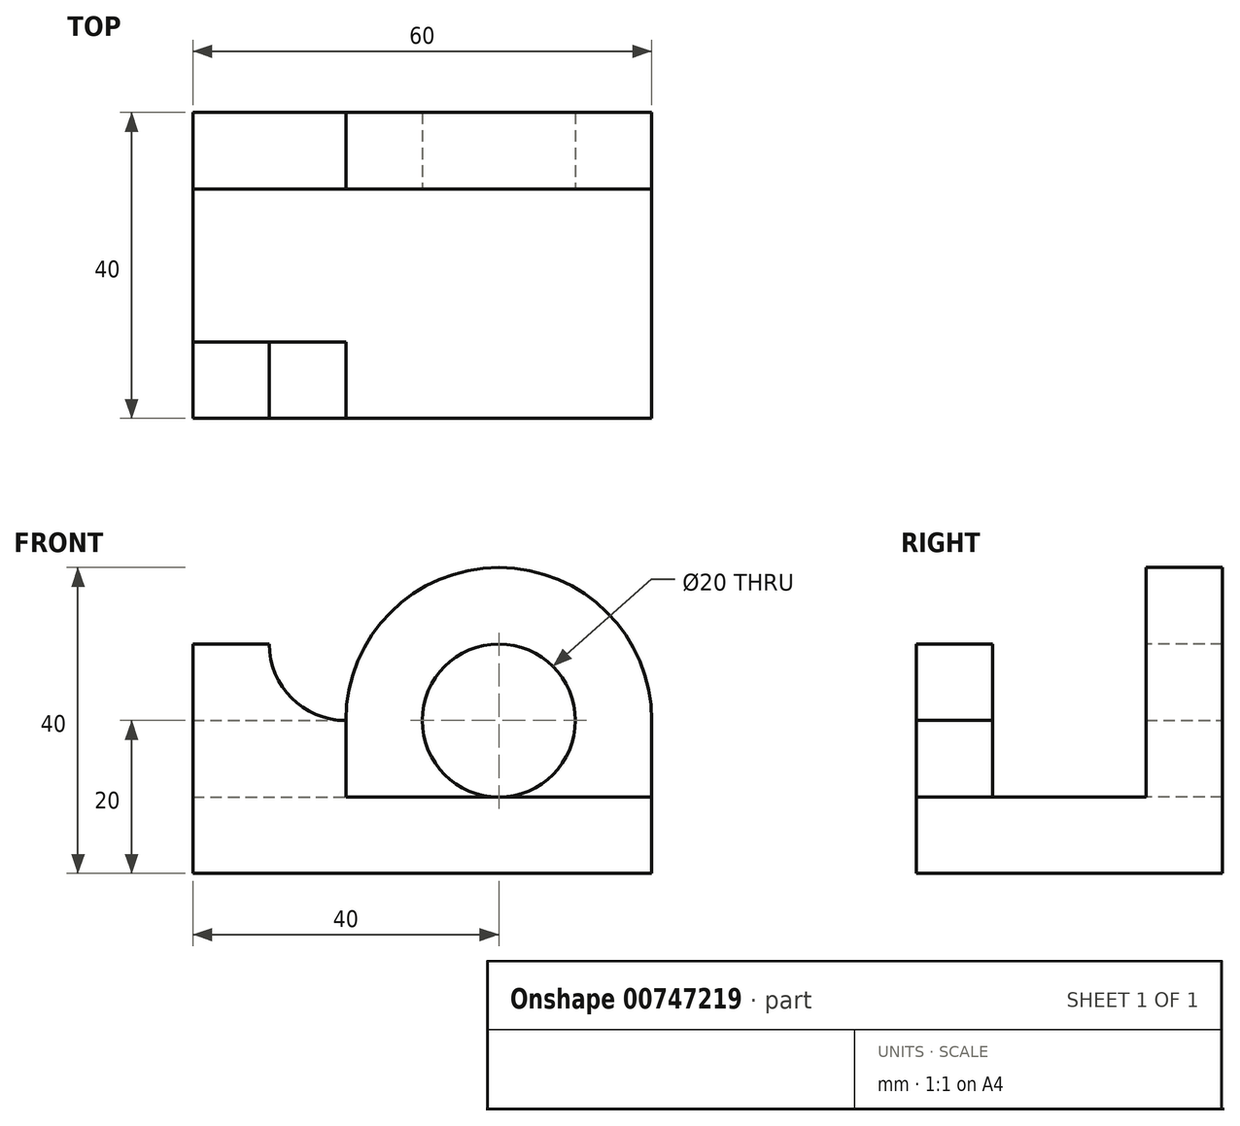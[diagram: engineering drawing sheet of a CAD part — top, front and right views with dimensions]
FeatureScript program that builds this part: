
annotation { "Feature Type Name" : "Feature", "Feature Type Description" : "" }
export const myFeature = defineFeature(function(context is Context, id is Id, definition is map)
    precondition{}
    {
        {
            var Q0;
            Q0=qCreatedBy(makeId("Front.planeOp"),FACE);
            var sketch = newSketch(context, id + "F0", { "sketchPlane" : qUnion([Q0])});
            skLineSegment(sketch, "E0", {"start": v(0, 0) * mm, "end": v(60, 0) * mm});
            skLineSegment(sketch, "E1", {"start": v(60, 0) * mm, "end": v(60, 40) * mm});
            skLineSegment(sketch, "E2", {"start": v(60, 40) * mm, "end": v(0, 40) * mm});
            skLineSegment(sketch, "E3", {"start": v(0, 40) * mm, "end": v(0, 0) * mm});
            skSolve(sketch);
        }
        {
            var Q0;
            Q0=makeQuery(id+"F0.imprint","IMPRINT",FACE,{"disambiguationData":[TD([[makeQuery(id+"F0.imprint","IMPRINT",EDGE,{"derivedFrom":sQuery(id+"F0.wireOp",EDGE,"E0")}),1.0]])]});
            extrude(context, id + "F1", {"entities" : qUnion([Q0]), "depth" : 40 * mm, "offsetDistance" : 25 * mm});
        }
        {
            var Q0;
            Q0=makeQuery(id+"F1.opExtrude","SWEPT_FACE",FACE,{"disambiguationData":[OSD([sQuery(id+"F0.wireOp",EDGE,"E1")])]});
            var sketch = newSketch(context, id + "F2", { "sketchPlane" : qUnion([Q0])});
            skLineSegment(sketch, "E4", {"start": v(-40, 40) * mm, "end": v(-40, 30) * mm});
            skLineSegment(sketch, "E5", {"start": v(-40, 30) * mm, "end": v(-30, 30) * mm});
            skLineSegment(sketch, "E6", {"start": v(-30, 30) * mm, "end": v(-30, 10) * mm});
            skLineSegment(sketch, "E7", {"start": v(-30, 10) * mm, "end": v(-10, 10) * mm});
            skLineSegment(sketch, "E8", {"start": v(-10, 10) * mm, "end": v(-10, 40) * mm});
            skLineSegment(sketch, "E9", {"start": v(-10, 40) * mm, "end": v(-40, 40) * mm});
            skSolve(sketch);
        }
        {
            var Q0;
            Q0=makeQuery(id+"F2.imprint","IMPRINT",FACE,{"disambiguationData":[TD([[makeQuery(id+"F2.imprint","IMPRINT",EDGE,{"derivedFrom":sQuery(id+"F2.wireOp",EDGE,"E4")}),-1.0]])]});
            extrude(context, id + "F3", {"entities" : qUnion([Q0]), "operationType" : NewBodyOperationType.REMOVE, "oppositeDirection" : true, "depth" : 60 * mm, "offsetDistance" : 25 * mm});
        }
        {
            var Q0;
            Q0=makeQuery(id+"F3.boolean.opBoolean","COPY",FACE,{"derivedFrom":makeQuery(id+"F3.opExtrude","SWEPT_FACE",FACE,{"disambiguationData":[OSD([sQuery(id+"F2.wireOp",EDGE,"E5")])]})});
            var sketch = newSketch(context, id + "F4", { "sketchPlane" : qUnion([Q0])});
            skLineSegment(sketch, "E10", {"start": v(60, -40) * mm, "end": v(60, -30) * mm});
            skLineSegment(sketch, "E11", {"start": v(60, -30) * mm, "end": v(20, -30) * mm});
            skLineSegment(sketch, "E12", {"start": v(20, -30) * mm, "end": v(20, -40) * mm});
            skLineSegment(sketch, "E13", {"start": v(20, -40) * mm, "end": v(60, -40) * mm});
            skSolve(sketch);
        }
        {
            var Q0;
            Q0=makeQuery(id+"F4.imprint","IMPRINT",FACE,{"disambiguationData":[TD([[makeQuery(id+"F4.imprint","IMPRINT",EDGE,{"derivedFrom":sQuery(id+"F4.wireOp",EDGE,"E10")}),1.0]])]});
            extrude(context, id + "F5", {"entities" : qUnion([Q0]), "operationType" : NewBodyOperationType.REMOVE, "oppositeDirection" : true, "depth" : 20 * mm, "offsetDistance" : 25 * mm});
        }
        {
            var Q0;
            Q0=makeQuery(id+"F1.opExtrude","CAP_FACE",FACE,{"disambiguationData":[OSD([sQuery(id+"F0.wireOp",EDGE,"E0"),sQuery(id+"F0.wireOp",EDGE,"E1"),sQuery(id+"F0.wireOp",EDGE,"E2"),sQuery(id+"F0.wireOp",EDGE,"E3")])],"isStart":false});
            var sketch = newSketch(context, id + "F6", { "sketchPlane" : qUnion([Q0])});
            skArc(sketch, "E14", {"start": v(10, 30) * mm, "mid": v(12.93, 22.93) * mm, "end": v(20, 20) * mm});
            skLineSegment(sketch, "E15", {"start": v(10, 30) * mm, "end": v(20, 30) * mm});
            skLineSegment(sketch, "E16", {"start": v(20, 20) * mm, "end": v(20, 30) * mm});
            skSolve(sketch);
        }
        {
            var Q0;
            Q0=makeQuery(id+"F6.imprint","IMPRINT",FACE,{"disambiguationData":[TD([[makeQuery(id+"F6.imprint","IMPRINT",EDGE,{"derivedFrom":sQuery(id+"F6.wireOp",EDGE,"E14")}),1.0]])]});
            extrude(context, id + "F7", {"entities" : qUnion([Q0]), "operationType" : NewBodyOperationType.ADD, "depth" : 10 * mm, "offsetDistance" : 25 * mm});
        }
        {
            var Q0;
            Q0=makeQuery(id+"F7.opExtrude","CAP_FACE",FACE,{"disambiguationData":[OSD([sQuery(id+"F6.wireOp",EDGE,"E14"),sQuery(id+"F6.wireOp",EDGE,"E15"),sQuery(id+"F6.wireOp",EDGE,"E16")])],"isStart":false});
            extrude(context, id + "F8", {"entities" : qUnion([Q0]), "operationType" : NewBodyOperationType.REMOVE, "oppositeDirection" : true, "depth" : 20 * mm, "offsetDistance" : 25 * mm});
        }
        {
            var Q0;
            Q0=makeQuery(id+"F1.opExtrude","CAP_FACE",FACE,{"disambiguationData":[OSD([sQuery(id+"F0.wireOp",EDGE,"E0"),sQuery(id+"F0.wireOp",EDGE,"E1"),sQuery(id+"F0.wireOp",EDGE,"E2"),sQuery(id+"F0.wireOp",EDGE,"E3")])],"isStart":true});
            var sketch = newSketch(context, id + "F9", { "sketchPlane" : qUnion([Q0])});
            skLineSegment(sketch, "E17", {"start": v(0, 40) * mm, "end": v(0, 20) * mm});
            skLineSegment(sketch, "E18", {"start": v(0, 20) * mm, "end": v(-20, 20) * mm});
            skLineSegment(sketch, "E19", {"start": v(-20, 20) * mm, "end": v(-20, 40) * mm});
            skLineSegment(sketch, "E20", {"start": v(-20, 40) * mm, "end": v(0, 40) * mm});
            skSolve(sketch);
        }
        {
            var Q0;
            Q0=makeQuery(id+"F9.imprint","IMPRINT",FACE,{"disambiguationData":[TD([[makeQuery(id+"F9.imprint","IMPRINT",EDGE,{"derivedFrom":sQuery(id+"F9.wireOp",EDGE,"E17")}),-1.0]])]});
            extrude(context, id + "F10", {"entities" : qUnion([Q0]), "operationType" : NewBodyOperationType.REMOVE, "oppositeDirection" : true, "depth" : 10 * mm, "offsetDistance" : 25 * mm});
        }
        {
            var Q0;
            Q0=makeQuery(id+"F3.boolean.opBoolean","COPY",FACE,{"derivedFrom":makeQuery(id+"F3.opExtrude","SWEPT_FACE",FACE,{"disambiguationData":[OSD([sQuery(id+"F2.wireOp",EDGE,"E8")])]})});
            var sketch = newSketch(context, id + "F11", { "sketchPlane" : qUnion([Q0])});
            skArc(sketch, "E21", {"start": v(60, 20) * mm, "mid": v(40, 40) * mm, "end": v(20, 20) * mm});
            skSolve(sketch);
        }
        {
            var Q0;
            {var subQ1=makeQuery(id+"F10.boolean.opBoolean","COPY",EDGE,{"derivedFrom":makeQuery(id+"F10.opExtrude","CAP_EDGE",EDGE,{"disambiguationData":[OSD([sQuery(id+"F9.wireOp",EDGE,"E19")])],"isStart":false})});Q0=makeQuery(id+"F11.imprint","IMPRINT",FACE,{"disambiguationData":[TD([[makeQuery(id+"F11.imprint","IMPRINT",EDGE,{"derivedFrom":subQ1}),-1.0]])]});}
            var Q1;
            {var subQ0=sQuery(id+"F11.wireOp",EDGE,"E21");var subQ1=sQuery(id+"F2.wireOp",EDGE,"E8");var subQ2=makeQuery(id+"F3.boolean.opBoolean","COPY",EDGE,{"derivedFrom":makeQuery(id+"F3.opExtrude","CAP_EDGE",EDGE,{"disambiguationData":[OSD([subQ1])],"isStart":true})});var subQ3=makeQuery(id+"F11.imprint","INTERSECT",VERTEX,{"derivedFrom":[subQ2,subQ0]});Q1=makeQuery(id+"F11.imprint","IMPRINT",FACE,{"disambiguationData":[TD([[makeQuery(id+"F11.imprint","IMPRINT",EDGE,{"disambiguationData":[TD([[subQ3,-1.0]])],"derivedFrom":subQ0}),-1.0]])]});}
            extrude(context, id + "F12", {"entities" : qUnion([Q0, Q1]), "operationType" : NewBodyOperationType.REMOVE, "oppositeDirection" : true, "depth" : 10 * mm, "offsetDistance" : 25 * mm});
        }
        {
            var Q0;
            Q0=makeQuery(id+"F3.boolean.opBoolean","COPY",FACE,{"derivedFrom":makeQuery(id+"F3.opExtrude","SWEPT_FACE",FACE,{"disambiguationData":[OSD([sQuery(id+"F2.wireOp",EDGE,"E8")])]})});
            var sketch = newSketch(context, id + "F13", { "sketchPlane" : qUnion([Q0])});
            skCircle(sketch, "E22", {"center": v(40, 20) * mm, "radius": 10 * mm});
            skSolve(sketch);
        }
        {
            var Q0;
            Q0=makeQuery(id+"F13.imprint","IMPRINT",FACE,{"disambiguationData":[TD([[makeQuery(id+"F13.imprint","IMPRINT",EDGE,{"derivedFrom":sQuery(id+"F13.wireOp",EDGE,"E22")}),1.0]])]});
            extrude(context, id + "F14", {"entities" : qUnion([Q0]), "operationType" : NewBodyOperationType.REMOVE, "oppositeDirection" : true, "depth" : 10 * mm, "offsetDistance" : 25 * mm});
        }
    });
